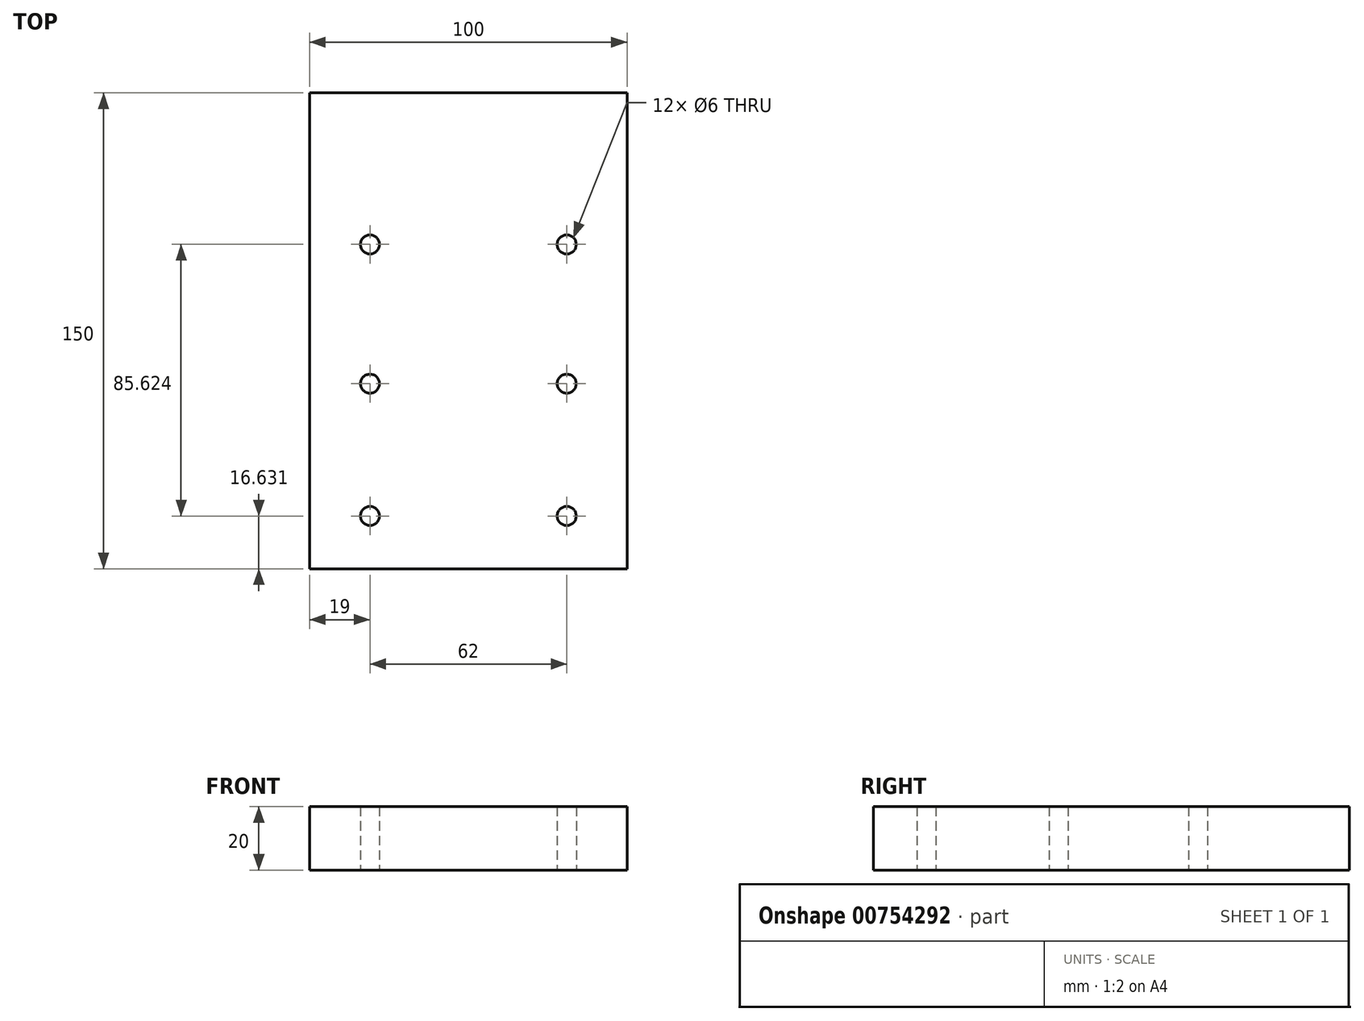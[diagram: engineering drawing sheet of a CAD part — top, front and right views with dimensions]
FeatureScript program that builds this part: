
annotation { "Feature Type Name" : "Feature", "Feature Type Description" : "" }
export const myFeature = defineFeature(function(context is Context, id is Id, definition is map)
    precondition{}
    {
        {
            var Q0;
            Q0=qCreatedBy(makeId("Top.planeOp"),FACE);
            var sketch = newSketch(context, id + "F0", { "sketchPlane" : qUnion([Q0])});
            skLineSegment(sketch, "E0.bottom", {"start": v(50, 75) * mm, "end": v(-50, 75) * mm});
            skLineSegment(sketch, "E0.top", {"start": v(50, -75) * mm, "end": v(-50, -75) * mm});
            skLineSegment(sketch, "E0.left", {"start": v(50, 75) * mm, "end": v(50, -75) * mm});
            skLineSegment(sketch, "E0.right", {"start": v(-50, 75) * mm, "end": v(-50, -75) * mm});
            skPoint(sketch, "E0.middle", {"position": v(0, 0) * mm});
            skPoint(sketch, "E1", {"position": v(-31, -58.37) * mm});
            skPoint(sketch, "E2", {"position": v(31, -58.37) * mm});
            skPoint(sketch, "E3", {"position": v(-31, -16.64) * mm});
            skPoint(sketch, "E4", {"position": v(-31, 27.25) * mm});
            skPoint(sketch, "E5", {"position": v(31, -16.64) * mm});
            skPoint(sketch, "E6", {"position": v(31, 27.25) * mm});
            skCircle(sketch, "E7", {"center": v(-31, 27.25) * mm, "radius": 3 * mm});
            skCircle(sketch, "E8", {"center": v(31, 27.25) * mm, "radius": 3 * mm});
            skCircle(sketch, "E9", {"center": v(-31, -16.64) * mm, "radius": 3 * mm});
            skCircle(sketch, "E10", {"center": v(31, -16.64) * mm, "radius": 3 * mm});
            skCircle(sketch, "E11", {"center": v(31, -58.37) * mm, "radius": 3 * mm});
            skCircle(sketch, "E12", {"center": v(-31, -58.37) * mm, "radius": 3 * mm});
            skSolve(sketch);
        }
        {
            var Q0;
            Q0 = qSketchRegion(id + "F0", true);
            extrude(context, id + "F1", {"entities" : qUnion([Q0]), "depth" : 20 * mm, "offsetDistance" : 25 * mm});
        }
    });
